# Revit family: UV Low Pressure - Reactor
name_source: partatom
category: Mechanical Equipment
units: mm (PartAtom-declared; Revit-internal decimal feet)

## family parameters
Always vertical = Yes
Cut with Voids When Loaded = No
OmniClass Number = 23.65.50.11
OmniClass Title = Water Treatment
Part Type = Normal
Room Calculation Point = No
Round Connector Dimension = Use Radius
Shared = No
Work Plane-Based = No

## types (4) — shared parameters
Assembly Code = D2090400
D = 40 3/16"
Description = Jandy Commercial Low-Pressure UV System
F = 14"
Fluidra_Description = Jandy Commercial Low-Pressure UV System
Fluidra_Manufacturer = Fluidra
Fluidra_Max_Rated_Pressure = 50.00 psi
G = 9 13/16"
Manufacturer = Fluidra
URL = https://www.jandy.com

## per-type parameters (varying)
| type | Center to Flange | E | Flange | Flange Adapter | Flange Diameter | Flange Gasket | Flange Plate | Flange Ring | Fluidra_#_Lamps | Fluidra_Max_Flow(UVT_94%) |
| JUVLP100 | 9 1/2" | 22 13/16" | Flange 3in | Flange Adapter 3in | 3" | Flange Gasket 3in | Flange Plate 3in | Flange Ring 3in | 3 | 105 GPM |
| JUVLP200 | 10" | 22 1/4" | Flange 4in | Flange Adapter 4in | 4" | Flange Gasket 4in | Flange Plate 4in | Flange Ring 4in | 5 | 175 GPM |
| JUVLP250 | 10" | 22 1/4" | Flange 4in | Flange Adapter 4in | 4" | Flange Gasket 4in | Flange Plate 4in | Flange Ring 4in | 6 | 210 GPM |
| JUVLP150 | 9 1/2" | 22 13/16" | Flange 3in | Flange Adapter 3in | 3" | Flange Gasket 3in | Flange Plate 3in | Flange Ring 3in | 4 | 140 GPM |

note: column(s) folded — value = type name in every type: Fluidra_Model, Model

## geometry (parser evidence)
native form markers: Sweep x36
no freeform markers — native parametric forms only
